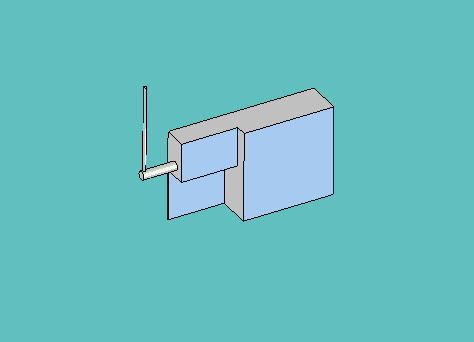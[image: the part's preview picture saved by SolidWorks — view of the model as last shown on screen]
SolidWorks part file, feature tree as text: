
SOLIDWORKS PART (.sldprt)
format: sldprt  version: not decoded by parser v0  size: 239,616 bytes
history: native  units: mm
features: sketch x5, extrude x5, material x1, plane x1 (+11 scaffold rows collapsed)
feature tree (23):
  scaffold x11  (default folders/planes/origin — collapsed)
  material  "Material <not specified>"
  sketch  "Sketch1"  dims[D1=50.8mm D2=101.6mm D3=19.05mm]
  extrude  "Extrude1"  Depth=0.79375mm
  sketch  "Sketch2"  dims[D1=50.8mm]
  extrude  "Extrude2"  Depth=19.05mm
  sketch  "Sketch3"  dims[c1.D1=22.225mm c1.D2=31.75mm c2.D1=22.225mm]
  extrude  "Extrude3"  Depth=12.7mm
  sketch  "Sketch4"  dims[D1=4.7625mm D2=6.35mm]
  extrude  "Extrude4"  Depth=19.05mm
  plane  "Plane1"
  sketch  "Sketch5"  dims[D1=1.5875mm D2=1.5875mm]
  extrude  "Extrude5"  Depth=50.8mm
decode coverage: 10 of 10 modeling features carry decoded parameters
note: suppression state not decoded; provenance and decode notes live in map.json
